# Revit family: TrashBox-WasteBin-Vitra-BaseSeries-A44151
name_source: partatom
category: Plumbing Fixtures
revit_build: Autodesk Revit 2017 (Build: 20160225_1515(x64)
units: mm (PartAtom-declared; Revit-internal decimal feet)

## family parameters
Cut with Voids When Loaded = No
Host = Face
OmniClass Number = 23.45.00.00
OmniClass Title = Sanitary, Laundry, and Cleaning Equipment
Part Type = Normal
Room Calculation Point = No
Round Connector Dimension = Use Diameter
Shared = Yes

## types (2) — shared parameters
BIMobject category = Sanitary - Accessories
Brand = VitrA
CW Connection = No
Coating Material = Plastic
Default Elevation = 850 mm  [stored 2.78871 ft]
Description = Bathroom Waste Bins
Design country = Turkey
HW Connection = No
IFC Classification = Furnishing Element
Main Material = Metal
Manufacturer = VitrA
Manufacturer name = VitrA
Masterformat 2014 Code = 11 82 13
Masterformat 2014 Description = Solid Waste Bins
Mounting type = Floor-Standing
NBS Referans Code = 35-10-97
NBS Referans Description = Waste Bins
Nominal Depth (mm) = 205 mm  [stored 0.672572 ft]
Nominal Height (mm) = 285 mm  [stored 0.935039 ft]
Nominal Width (mm) = 205 mm  [stored 0.672572 ft]
OmniClass Code = 23-21 17 11
OmniClass Description = Interior Waste Bins
Product Type = Waste Bins
Product certification = https://www.vitraglobal.com
Product family = Base Series
Product group = Bathroom Waste Bins
Product manual = Trash Box
Product url = https://www.vitraglobal.com
Technical description = https://www.vitraglobal.com
UNSPSC Code = 56
UNSPSC Description = Furniture and Furnishings
URL = https://www.vitraglobal.com
Uniclass 1.4 Code = L7235
Uniclass 1.4 Description = Waste disposal units
Uniclass 2.0 Code = PR-35-10-97
Uniclass 2.0 Description = Waste Bins
Uniclass 2015 Code = Pr_40_50_07_96
Uniclass 2015 Name = Waste bins
Uniformat II Description = EQUIPMENT & FURNISHINGS
Vent Connection = No
Warranty Period (Year) = 2
Waste Connection = No
Youtube = https://www.youtube.com

## per-type parameters (varying)
| type | Article No. (default) | Calculated flow | Model | Primary Material | Product SKU |
| TrashBox-WasteBin-Vitra-BaseSeries-A44151 | A44151 | White/Chrome | A44151 | Chrome | A44151 |
| TrashBox-WasteBin-Vitra-BaseSeries-A4415136 | A4415136 | Matte Black | A4415136 | Matte Black (Metal) | A4415136 |

note: [stored X ft] marks values corroborated as IEEE doubles in the binary element streams (Revit-internal decimal feet)

## geometry (parser evidence)
native form markers: Sweep x3
no freeform markers — native parametric forms only
